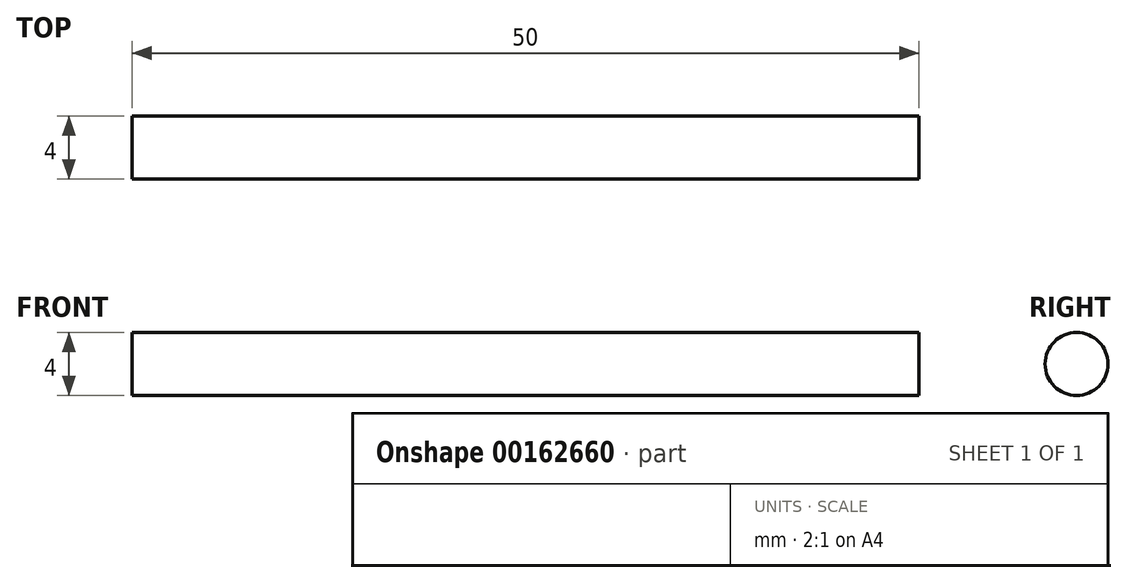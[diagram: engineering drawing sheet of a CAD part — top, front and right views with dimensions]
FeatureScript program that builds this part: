
annotation { "Feature Type Name" : "Feature", "Feature Type Description" : "" }
export const myFeature = defineFeature(function(context is Context, id is Id, definition is map)
    precondition{}
    {
        {
            var Q0;
            Q0=qCreatedBy(makeId("Right.planeOp"),FACE);
            var sketch = newSketch(context, id + "F0", { "sketchPlane" : qUnion([Q0])});
            skCircle(sketch, "E0", {"center": v(0, 0) * mm, "radius": 2 * mm});
            skSolve(sketch);
        }
        {
            var Q0;
            Q0 = qSketchRegion(id + "F0", true);
            extrude(context, id + "F1", {"entities" : qUnion([Q0]), "depth" : 50 * mm, "offsetDistance" : 25 * mm});
        }
    });
